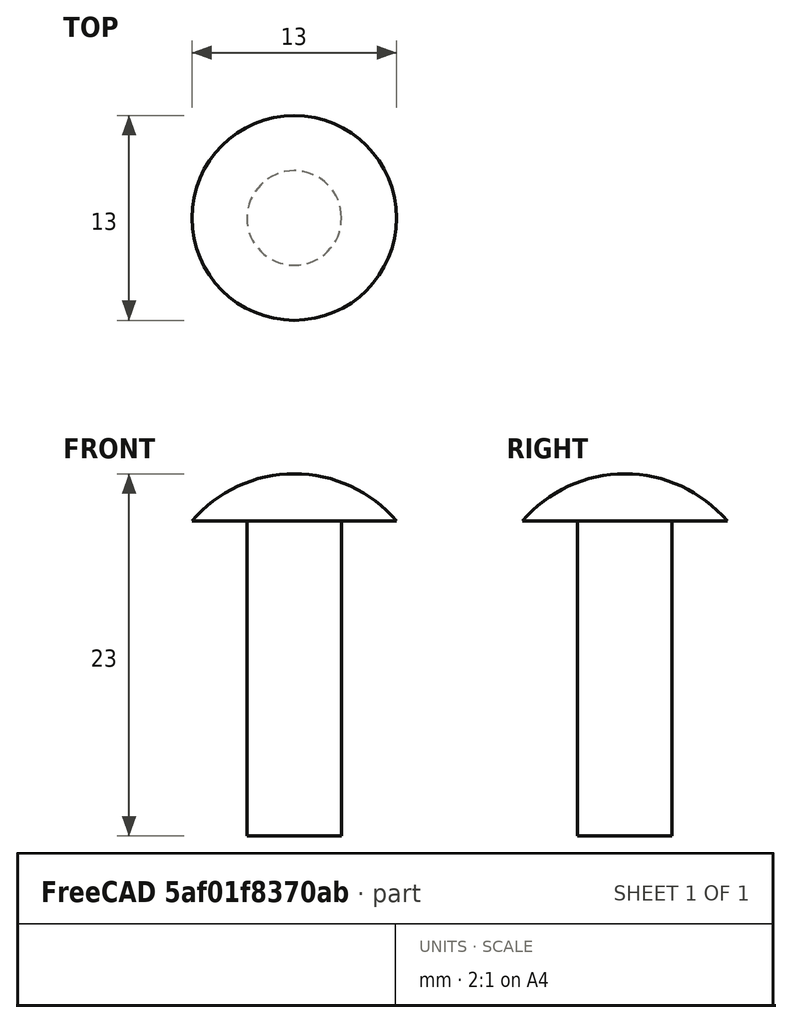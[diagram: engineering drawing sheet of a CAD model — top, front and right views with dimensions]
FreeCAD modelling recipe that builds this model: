
FCSTD DOCUMENT  (FreeCAD 0.18R14555 (Git shallow))
Label: m6-20
License: All rights reserved
LicenseURL: http://en.wikipedia.org/wiki/All_rights_reserved
objects: Sketcher::SketchObject×1, PartDesign::Revolution×1, PartDesign::Body×1
note: 4 computed .brp shape members not serialized (recipe doc carries the construction recipe); baked Part::Feature solids carry a one-line shape summary decoded from their .brp

FEATURE [Sketcher::SketchObject] Sketch
  MapMode = 5
  Placement = pos=(0,0,0) rot=(1,0,0;1.5708rad)
  Support = -> [XZ_Plane]
  sketch-geometry (5):
    g0: LineSegment StartX=0 StartY=23 StartZ=0 EndX=0 EndY=0 EndZ=0
    g1: LineSegment StartX=0 StartY=0 StartZ=0 EndX=3 EndY=0 EndZ=0
    g2: ArcOfCircle CenterX=0 CenterY=14.4583 CenterZ=0 NormalX=0 NormalY=0 NormalZ=1 AngleXU=0 Radius=8.54167 StartAngle=0.705981 EndAngle=1.5708
    g3: LineSegment StartX=3 StartY=0 StartZ=0 EndX=3 EndY=20 EndZ=0
    g4: LineSegment StartX=3 StartY=20 StartZ=0 EndX=6.5 EndY=20 EndZ=0
  constraints (15):
    c: Vertical(g0)
    c: Coincident(g0,g1)
    c: Horizontal(g1)
    c: Coincident(g2,g0)
    c: Coincident(g1,g3)
    c: Vertical(g3)
    c: Coincident(g3,g4)
    c: Coincident(g4,g2)
    c: Horizontal(g4)
    c: Coincident(g0,g-1)
    c: DistanceX(g1,g1) = 3
    c: DistanceX(g0,g2) = 6.5
    c: DistanceY(g3,g3) = 20
    c: DistanceY(g3,g0) = 3
    c: Perpendicular(g2,g0)
FEATURE [PartDesign::Revolution] Revolution
  Angle = 360
  Axis = (0,2e-16,1)
  Base = (0,0,0)
  Placement = pos=(0,0,0) rot=(1,0,0;1.5708rad)
  Profile = -> Sketch
  ReferenceAxis = -> Sketch [V_Axis]
  Reversed = true
FEATURE [PartDesign::Body] Body
  Group = -> [Sketch,Revolution]
  Origin = -> Origin
  Tip = -> Revolution
